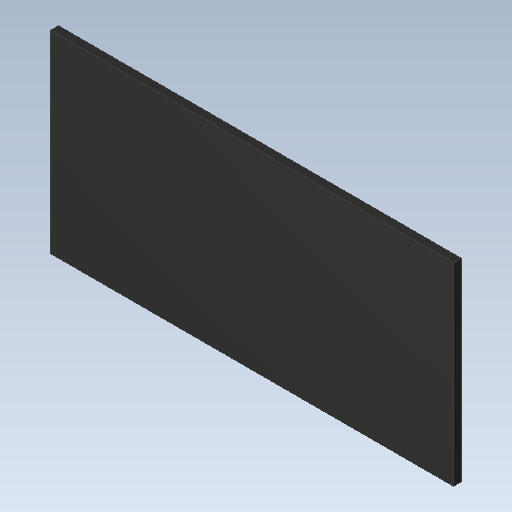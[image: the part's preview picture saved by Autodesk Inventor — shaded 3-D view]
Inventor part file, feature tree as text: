
AUTODESK INVENTOR PART (.ipt)
format: ipt  version: 2020 (Build 240168000, 168)  size: 87,040 bytes
history: imported  units: in
note: dims shown in document units (in); Inventor stores cm internally (conversion verified against a paired STEP export)
features: imported_body x1
ambient origin geometry x8: Origin, YZ Plane, XZ Plane, XY Plane, X Axis, Y Axis, Z Axis, Center Point
bodies: Solid1 (imported_parasolid), Body1 (imported_parasolid)
feature tree (1):
  imported_body  NMx_Import_Brep_tag  [imported B-rep: ~6 faces, bbox_mm=[5.1816, 2.4892, 0.1]]
